# Revit family: Automatic_Hand_Dryer-Bobrick-Puredri-B-9100_Series
name_source: partatom
category: Electrical Fixtures
units: mm (PartAtom-declared; Revit-internal decimal feet)

## family parameters
Cut with Voids When Loaded = No
Host = Face
Maintain Annotation Orientation = No
OmniClass Number = 23.40.20.21.14
OmniClass Title = Hand and Hair Dryers
Part Type = Normal
Room Calculation Point = No
Round Connector Dimension = Use Diameter
Shared = Yes

## types (1)
- B-9100
    115 Volt Models = No
    208-240 Volt Models = Yes
    ADA Compliant = Yes
    Assembly Code = C1030200
    Default Elevation = 40"
    Description = PureDri Automatic Hand Dryer and Air/Hand Sanitizer
    Dry Time = 12 Second
    Energy Consumption = 200 Watts
    Finish = Stainless_Steel-Bobrick-Type_304-Satin_Finish
    Height = 32 1/4"
    Installation Type = Wall Mounted
    Length = 4"
    Manufacturer = Bobrick
    Material = Stainless Steel-Bobrick-Satin Finish
    Model = B-9100
    Motor Operation = 40,000 RPM
    Motor Power = 24 Vdc
    Price = Prices may vary. Please consult Manufacturer Representative for most up-to-date price list.
    Sanitizing Time = 8 Second
    URL = https://www.bobrick.com
    Universal Voltage = 110V - 240V, 1.7AMP, 50/60Hz, 115 Volts, 0.2 kW.
    Voltage = 208-240 Volts
    Voltage Power = 240 V
    Warranty Information = 5-Year Limited Warranty
    Width = 10 1/2"

## geometry (parser evidence)
native form markers: Sweep x3
no freeform markers — native parametric forms only
